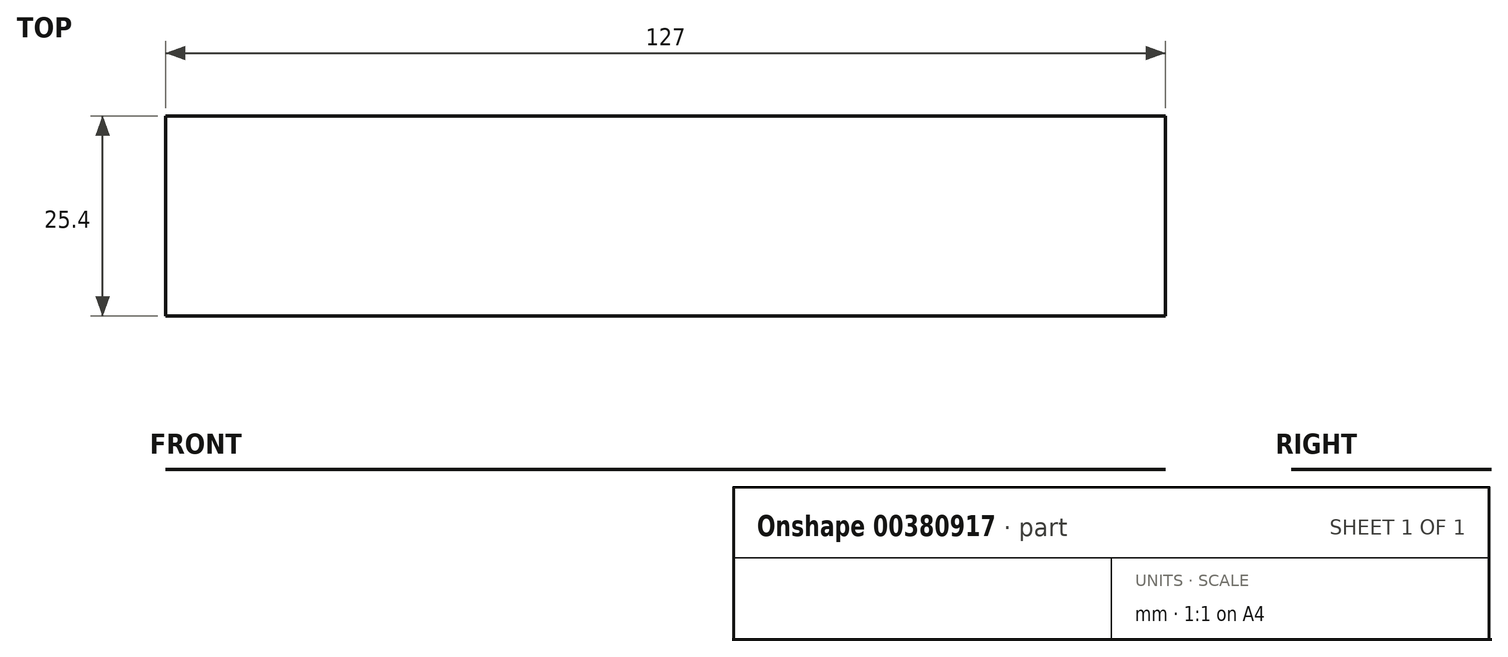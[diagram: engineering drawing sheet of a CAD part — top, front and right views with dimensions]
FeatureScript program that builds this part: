
annotation { "Feature Type Name" : "Feature", "Feature Type Description" : "" }
export const myFeature = defineFeature(function(context is Context, id is Id, definition is map)
    precondition{}
    {
        {
            var Q0;
            Q0=qCreatedBy(makeId("Front.planeOp"),FACE);
            var sketch = newSketch(context, id + "F0", { "sketchPlane" : qUnion([Q0])});
            skLineSegment(sketch, "E0", {"start": v(-97.39, 113.43) * mm, "end": v(-97.39, -44.19) * mm});
            skLineSegment(sketch, "E1", {"start": v(-97.39, -44.19) * mm, "end": v(29.61, -44.19) * mm});
            skLineSegment(sketch, "E2", {"start": v(29.61, -44.19) * mm, "end": v(29.61, 113.43) * mm});
            skLineSegment(sketch, "E3", {"start": v(29.61, 113.43) * mm, "end": v(-97.39, 113.43) * mm});
            skSolve(sketch);
        }
        {
            var Q0;
            Q0=sQuery(id+"F0.wireOp",EDGE,"E3");
            extrude(context, id + "F1", {"bodyType" : ToolBodyType.SURFACE, "surfaceEntities" : qUnion([Q0]), "depth" : 25.4 * mm, "offsetDistance" : 25.4 * mm});
        }
    });
